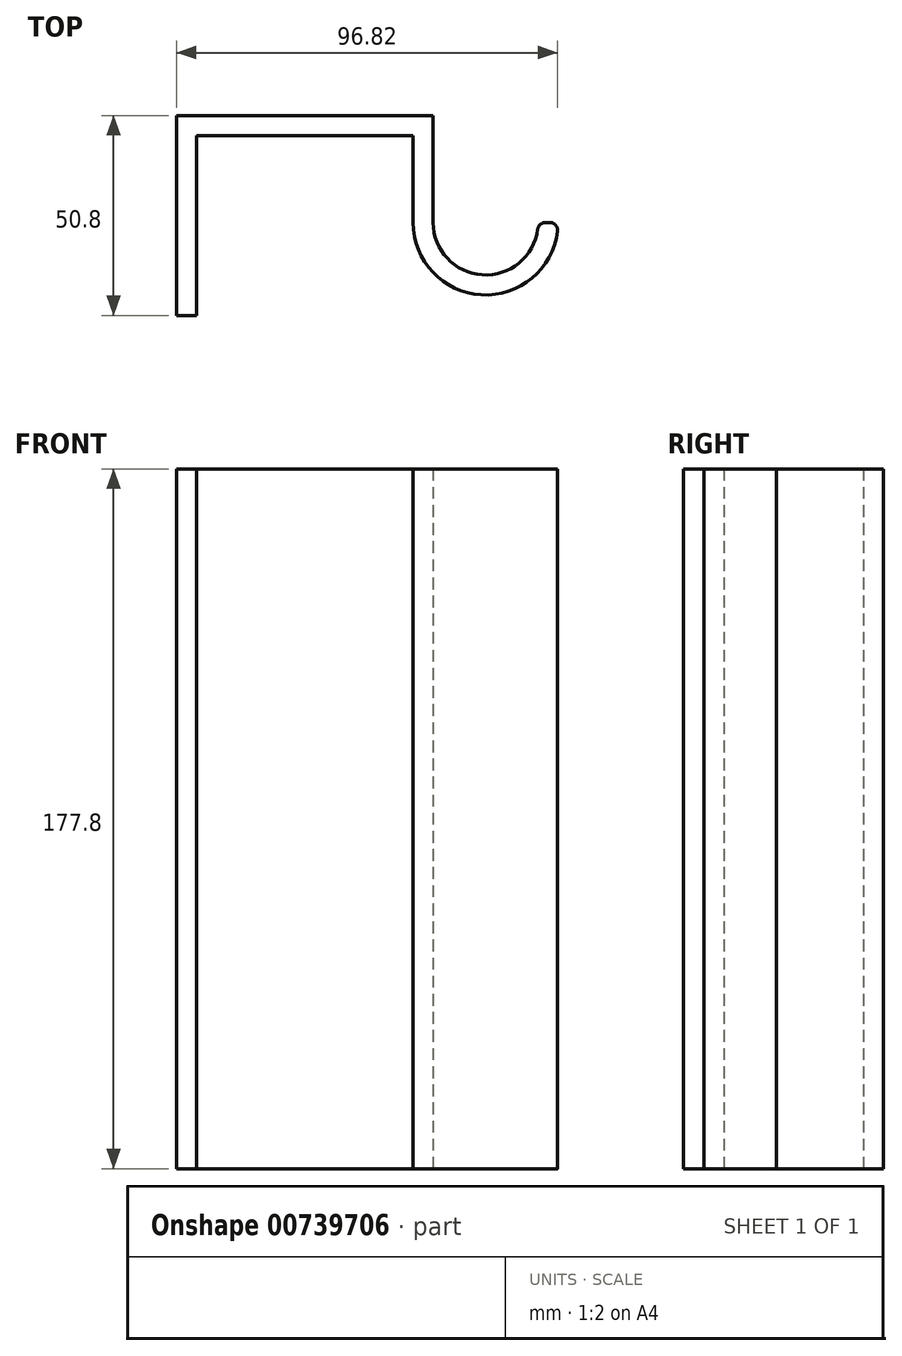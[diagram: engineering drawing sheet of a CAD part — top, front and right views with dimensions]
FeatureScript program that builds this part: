
annotation { "Feature Type Name" : "Feature", "Feature Type Description" : "" }
export const myFeature = defineFeature(function(context is Context, id is Id, definition is map)
    precondition{}
    {
        {
            var Q0;
            Q0=qCreatedBy(makeId("Top.planeOp"),FACE);
            var sketch = newSketch(context, id + "F0", { "sketchPlane" : qUnion([Q0])});
            skLineSegment(sketch, "E0", {"start": v(0, 0) * mm, "end": v(0, 45.72) * mm});
            skLineSegment(sketch, "E1", {"start": v(0, 45.72) * mm, "end": v(55, 45.72) * mm});
            skLineSegment(sketch, "E2", {"start": v(55, 45.72) * mm, "end": v(55, 23.61) * mm});
            skArc(sketch, "E3", {"start": v(55, 23.61) * mm, "mid": v(73.43, 5.18) * mm, "end": v(91.86, 23.61) * mm});
            skLineSegment(sketch, "E4", {"start": v(0, 0) * mm, "end": v(-5.08, 0) * mm});
            skLineSegment(sketch, "E5", {"start": v(-5.08, 0) * mm, "end": v(-5.08, 50.8) * mm});
            skLineSegment(sketch, "E6", {"start": v(-5.08, 50.8) * mm, "end": v(60.08, 50.8) * mm});
            skLineSegment(sketch, "E7", {"start": v(60.08, 50.8) * mm, "end": v(60.08, 23.61) * mm});
            skArc(sketch, "E8", {"start": v(60.08, 23.61) * mm, "mid": v(73.43, 10.26) * mm, "end": v(86.78, 23.61) * mm});
            skLineSegment(sketch, "E9", {"start": v(86.78, 23.61) * mm, "end": v(91.86, 23.61) * mm});
            skSolve(sketch);
        }
        {
            var Q0;
            Q0 = qSketchRegion(id + "F0", true);
            extrude(context, id + "F1", {"entities" : qUnion([Q0]), "depth" : 177.8 * mm, "offsetDistance" : 25.4 * mm});
        }
        {
            var Q0;
            Q0=makeQuery(id+"F1.opExtrude","SWEPT_EDGE",EDGE,{"disambiguationData":[OSD([sQuery(id+"F0.wireOp",EDGE,"E8"),sQuery(id+"F0.wireOp",EDGE,"E9")])]});
            var Q1;
            Q1=makeQuery(id+"F1.opExtrude","SWEPT_EDGE",EDGE,{"disambiguationData":[OSD([sQuery(id+"F0.wireOp",EDGE,"E3"),sQuery(id+"F0.wireOp",EDGE,"E9")])]});
            fillet(context, id + "F2", {"entities" : qUnion([Q0, Q1]), "radius" : 2 * mm, "tangentPropagation" : true, "allowEdgeOverflow" : false});
        }
    });
